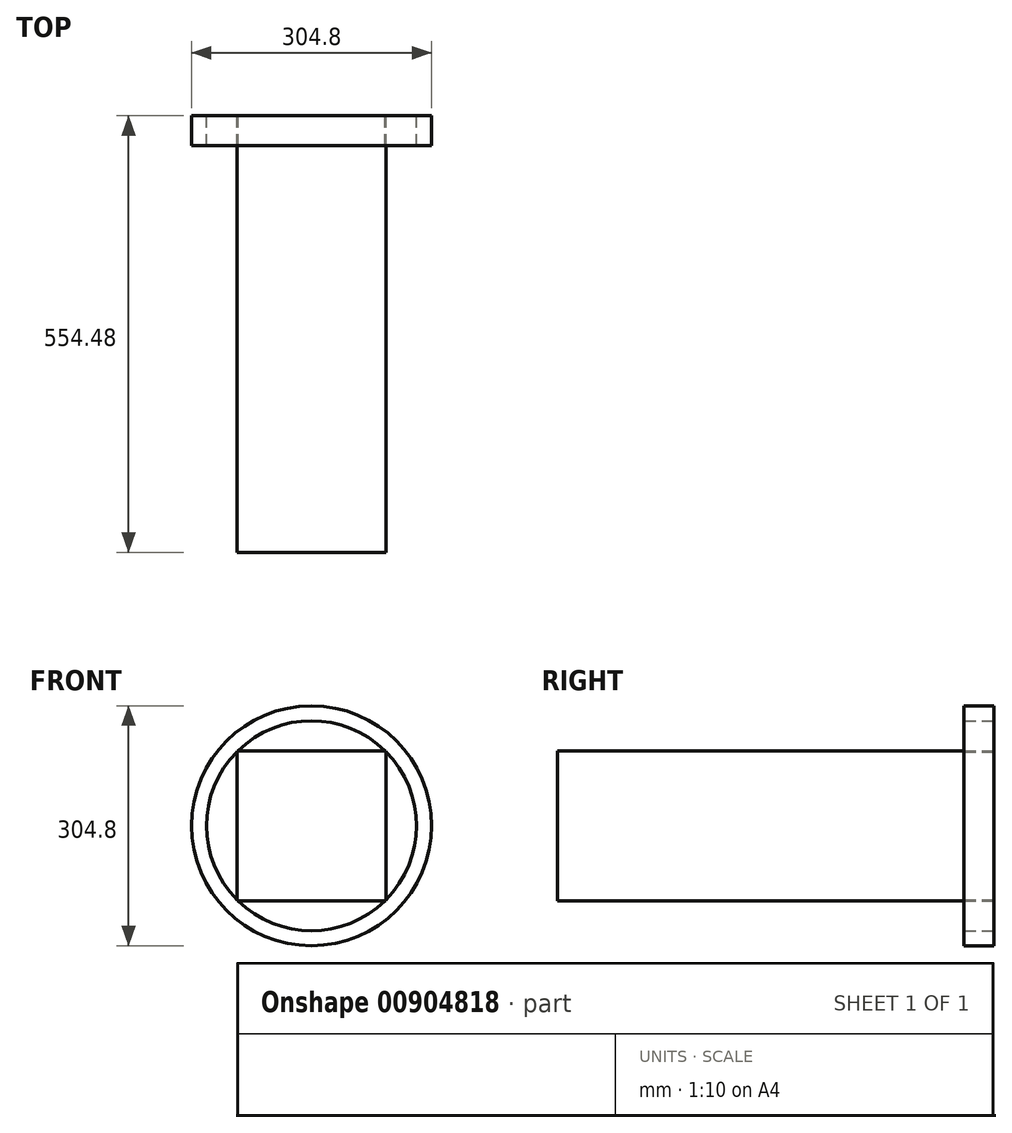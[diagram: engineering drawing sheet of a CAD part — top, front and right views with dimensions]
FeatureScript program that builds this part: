
annotation { "Feature Type Name" : "Feature", "Feature Type Description" : "" }
export const myFeature = defineFeature(function(context is Context, id is Id, definition is map)
    precondition{}
    {
        {
            var Q0;
            Q0=qCreatedBy(makeId("Front.planeOp"),FACE);
            var sketch = newSketch(context, id + "F0", { "sketchPlane" : qUnion([Q0])});
            skLineSegment(sketch, "E0.bottom", {"start": v(107.95, -76.2) * mm, "end": v(-107.95, -76.2) * mm});
            skLineSegment(sketch, "E0.top", {"start": v(107.95, 76.2) * mm, "end": v(-107.95, 76.2) * mm});
            skLineSegment(sketch, "E0.left", {"start": v(107.95, -76.2) * mm, "end": v(107.95, 76.2) * mm});
            skLineSegment(sketch, "E0.right", {"start": v(-107.95, -76.2) * mm, "end": v(-107.95, 76.2) * mm});
            skPoint(sketch, "E0.middle", {"position": v(0, 0) * mm});
            skCircle(sketch, "E1", {"center": v(0, 0) * mm, "radius": 133.35 * mm});
            skCircle(sketch, "E2", {"center": v(0, 0) * mm, "radius": 152.4 * mm});
            skSolve(sketch);
        }
        {
            var Q0;
            Q0=makeQuery(id+"F0.imprint","IMPRINT",FACE,{"disambiguationData":[TD([[makeQuery(id+"F0.imprint","IMPRINT",EDGE,{"derivedFrom":sQuery(id+"F0.wireOp",EDGE,"E1")}),-1.0]])]});
            extrude(context, id + "F1", {"entities" : qUnion([Q0]), "depth" : 38.1 * mm, "offsetDistance" : 25.4 * mm});
        }
        {
            var Q0;
            Q0=qCreatedBy(makeId("Front.planeOp"),FACE);
            var sketch = newSketch(context, id + "F2", { "sketchPlane" : qUnion([Q0])});
            skLineSegment(sketch, "E3.bottom", {"start": v(-94.53, -95.25) * mm, "end": v(94.53, -95.25) * mm});
            skLineSegment(sketch, "E3.top", {"start": v(-94.53, 95.25) * mm, "end": v(94.53, 95.25) * mm});
            skLineSegment(sketch, "E3.left", {"start": v(-94.53, -95.25) * mm, "end": v(-94.53, 95.25) * mm});
            skLineSegment(sketch, "E3.right", {"start": v(94.53, -95.25) * mm, "end": v(94.53, 95.25) * mm});
            skPoint(sketch, "E3.middle", {"position": v(0, 0) * mm});
            skSolve(sketch);
        }
        {
            var Q0;
            Q0 = qSketchRegion(id + "F2", true);
            extrude(context, id + "F3", {"entities" : qUnion([Q0]), "operationType" : NewBodyOperationType.ADD, "depth" : 554.48 * mm, "offsetDistance" : 25.4 * mm});
        }
    });
